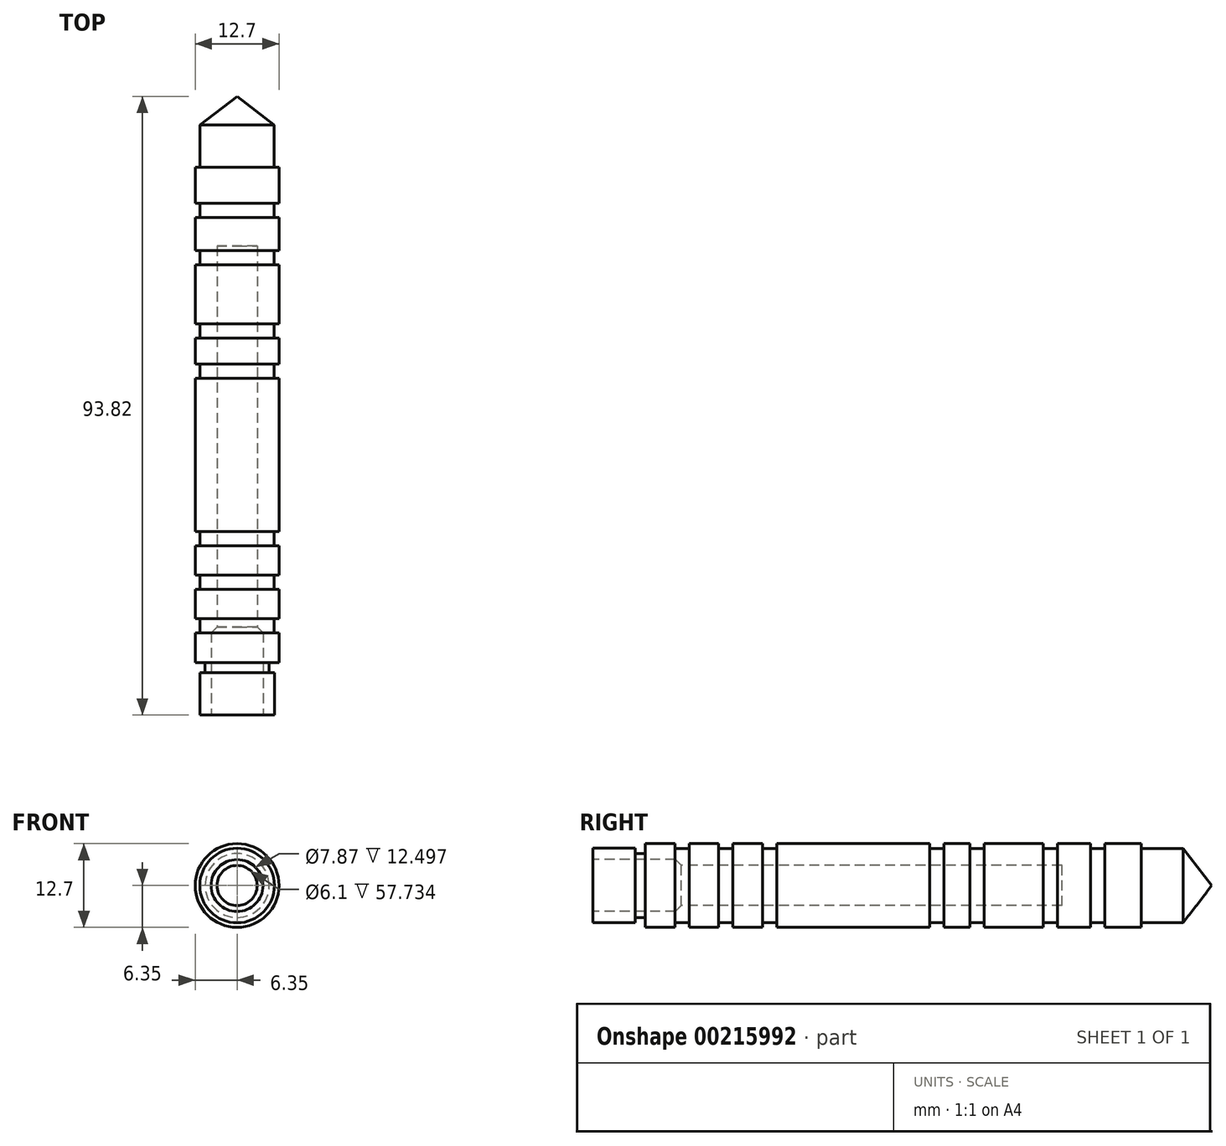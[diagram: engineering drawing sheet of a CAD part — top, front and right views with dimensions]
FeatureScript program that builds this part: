
annotation { "Feature Type Name" : "Feature", "Feature Type Description" : "" }
export const myFeature = defineFeature(function(context is Context, id is Id, definition is map)
    precondition{}
    {
        {
            var Q0;
            Q0=qCreatedBy(makeId("Front.planeOp"),FACE);
            var sketch = newSketch(context, id + "F0", { "sketchPlane" : qUnion([Q0])});
            skCircle(sketch, "E0", {"center": v(0, 0) * mm, "radius": 6.35 * mm});
            skSolve(sketch);
        }
        {
            var Q0;
            Q0 = qSketchRegion(id + "F0", true);
            extrude(context, id + "F1", {"entities" : qUnion([Q0]), "depth" : 93.83 * mm, "symmetric" : true});
        }
        {
            var Q0;
            Q0=makeQuery(id+"F1.opExtrude","CAP_FACE",FACE,{"disambiguationData":[OSD([sQuery(id+"F0.wireOp",EDGE,"E0")])],"isStart":false});
            var sketch = newSketch(context, id + "F2", { "sketchPlane" : qUnion([Q0])});
            skCircle(sketch, "E1", {"center": v(0, 0) * mm, "radius": 3.05 * mm});
            skSolve(sketch);
        }
        {
            var Q0;
            Q0 = qSketchRegion(id + "F2", true);
            extrude(context, id + "F3", {"entities" : qUnion([Q0]), "operationType" : NewBodyOperationType.REMOVE, "oppositeDirection" : true, "depth" : 71.12 * mm});
        }
        {
            var Q0;
            Q0=makeQuery(id+"F1.opExtrude","CAP_FACE",FACE,{"disambiguationData":[OSD([sQuery(id+"F0.wireOp",EDGE,"E0")])],"isStart":false});
            var sketch = newSketch(context, id + "F4", { "sketchPlane" : qUnion([Q0])});
            skCircle(sketch, "E2", {"center": v(0, 0) * mm, "radius": 3.94 * mm});
            skSolve(sketch);
        }
        {
            var Q0;
            Q0 = qSketchRegion(id + "F4", true);
            extrude(context, id + "F5", {"entities" : qUnion([Q0]), "operationType" : NewBodyOperationType.REMOVE, "oppositeDirection" : true, "depth" : 12.37 * mm});
        }
        {
            var Q0;
            Q0=makeQuery(id+"F1.opExtrude","CAP_FACE",FACE,{"disambiguationData":[OSD([sQuery(id+"F0.wireOp",EDGE,"E0")])],"isStart":false});
            var sketch = newSketch(context, id + "F6", { "sketchPlane" : qUnion([Q0])});
            skCircle(sketch, "E3", {"center": v(0, 0) * mm, "radius": 6.35 * mm});
            skCircle(sketch, "E4", {"center": v(0, 0) * mm, "radius": 5.65 * mm});
            skSolve(sketch);
        }
        {
            var Q0;
            Q0 = qSketchRegion(id + "F6", true);
            extrude(context, id + "F7", {"entities" : qUnion([Q0]), "operationType" : NewBodyOperationType.REMOVE, "oppositeDirection" : true, "depth" : 6.45 * mm});
        }
        {
            var Q0;
            Q0=makeQuery(id+"F7.boolean.opBoolean","COPY",FACE,{"derivedFrom":makeQuery(id+"F7.opExtrude","CAP_FACE",FACE,{"disambiguationData":[OSD([sQuery(id+"F6.wireOp",EDGE,"E3"),sQuery(id+"F6.wireOp",EDGE,"E4")])],"isStart":false})});
            var sketch = newSketch(context, id + "F8", { "sketchPlane" : qUnion([Q0])});
            skCircle(sketch, "E5", {"center": v(0, 0) * mm, "radius": 6.35 * mm});
            skCircle(sketch, "E6", {"center": v(0, 0) * mm, "radius": 4.85 * mm});
            skSolve(sketch);
        }
        {
            var Q0;
            Q0 = qSketchRegion(id + "F8", true);
            extrude(context, id + "F9", {"entities" : qUnion([Q0]), "operationType" : NewBodyOperationType.REMOVE, "oppositeDirection" : true, "depth" : 1.52 * mm});
        }
        {
            var Q0;
            Q0=makeQuery(id+"F5.boolean.opBoolean","INTERSECT",EDGE,{"derivedFrom":[makeQuery(id+"F3.boolean.opBoolean","COPY",FACE,{"derivedFrom":makeQuery(id+"F3.opExtrude","SWEPT_FACE",FACE,{"disambiguationData":[OSD([sQuery(id+"F2.wireOp",EDGE,"E1")])]})}),makeQuery(id+"F5.opExtrude","CAP_FACE",FACE,{"disambiguationData":[OSD([sQuery(id+"F4.wireOp",EDGE,"E2")])],"isStart":false})]});
            chamfer(context, id + "F10", {"entities" : qUnion([Q0]), "width" : 1.02 * mm, "tangentPropagation" : true});
        }
        {
            var Q0;
            Q0=makeQuery(id+"F9.boolean.opBoolean","COPY",FACE,{"derivedFrom":makeQuery(id+"F9.opExtrude","CAP_FACE",FACE,{"disambiguationData":[OSD([sQuery(id+"F8.wireOp",EDGE,"E5"),sQuery(id+"F8.wireOp",EDGE,"E6")])],"isStart":false})});
            cPlane(context, id + "F11", {"entities" : qUnion([Q0]), "cplaneType" : CPlaneType.OFFSET, "offset" : 4.47 * mm, "oppositeDirection" : true, "width" : 152.4 * mm, "height" : 152.4 * mm});
        }
        {
            var Q0;
            Q0=qCreatedBy(id+"F11.planeOp",FACE);
            var sketch = newSketch(context, id + "F12", { "sketchPlane" : qUnion([Q0])});
            skCircle(sketch, "E7", {"center": v(0, 0) * mm, "radius": 6.35 * mm});
            skCircle(sketch, "E8", {"center": v(0, 0) * mm, "radius": 5.61 * mm});
            skSolve(sketch);
        }
        {
            var Q0;
            Q0 = qSketchRegion(id + "F12", true);
            extrude(context, id + "F13", {"entities" : qUnion([Q0]), "operationType" : NewBodyOperationType.REMOVE, "oppositeDirection" : true, "depth" : 2.16 * mm});
        }
        {
            var Q0;
            Q0=makeQuery(id+"F13.boolean.opBoolean","COPY",FACE,{"derivedFrom":makeQuery(id+"F13.opExtrude","CAP_FACE",FACE,{"disambiguationData":[OSD([sQuery(id+"F12.wireOp",EDGE,"E7"),sQuery(id+"F12.wireOp",EDGE,"E8")])],"isStart":false})});
            cPlane(context, id + "F14", {"entities" : qUnion([Q0]), "cplaneType" : CPlaneType.OFFSET, "offset" : 4.47 * mm, "oppositeDirection" : true, "width" : 152.4 * mm, "height" : 152.4 * mm});
        }
        {
            var Q0;
            Q0=qCreatedBy(id+"F14.planeOp",FACE);
            var sketch = newSketch(context, id + "F15", { "sketchPlane" : qUnion([Q0])});
            skCircle(sketch, "E9", {"center": v(0, 0) * mm, "radius": 6.35 * mm});
            skCircle(sketch, "E10", {"center": v(0, 0) * mm, "radius": 5.61 * mm});
            skSolve(sketch);
        }
        {
            var Q0;
            Q0 = qSketchRegion(id + "F15", true);
            extrude(context, id + "F16", {"entities" : qUnion([Q0]), "operationType" : NewBodyOperationType.REMOVE, "oppositeDirection" : true, "depth" : 2.16 * mm});
        }
        {
            var Q0;
            Q0=makeQuery(id+"F16.boolean.opBoolean","COPY",FACE,{"derivedFrom":makeQuery(id+"F16.opExtrude","CAP_FACE",FACE,{"disambiguationData":[OSD([sQuery(id+"F15.wireOp",EDGE,"E9"),sQuery(id+"F15.wireOp",EDGE,"E10")])],"isStart":false})});
            cPlane(context, id + "F17", {"entities" : qUnion([Q0]), "cplaneType" : CPlaneType.OFFSET, "offset" : 4.47 * mm, "oppositeDirection" : true, "width" : 152.4 * mm, "height" : 152.4 * mm});
        }
        {
            var Q0;
            Q0=qCreatedBy(id+"F17.planeOp",FACE);
            var sketch = newSketch(context, id + "F18", { "sketchPlane" : qUnion([Q0])});
            skCircle(sketch, "E11", {"center": v(0, 0) * mm, "radius": 6.35 * mm});
            skCircle(sketch, "E12", {"center": v(0, 0) * mm, "radius": 5.61 * mm});
            skSolve(sketch);
        }
        {
            var Q0;
            Q0 = qSketchRegion(id + "F18", true);
            extrude(context, id + "F19", {"entities" : qUnion([Q0]), "operationType" : NewBodyOperationType.REMOVE, "oppositeDirection" : true, "depth" : 2.16 * mm});
        }
        {
            var Q0;
            Q0=makeQuery(id+"F19.boolean.opBoolean","COPY",FACE,{"derivedFrom":makeQuery(id+"F19.opExtrude","CAP_FACE",FACE,{"disambiguationData":[OSD([sQuery(id+"F18.wireOp",EDGE,"E11"),sQuery(id+"F18.wireOp",EDGE,"E12")])],"isStart":false})});
            cPlane(context, id + "F20", {"entities" : qUnion([Q0]), "cplaneType" : CPlaneType.OFFSET, "offset" : 23.2 * mm, "oppositeDirection" : true, "width" : 152.4 * mm, "height" : 152.4 * mm});
        }
        {
            var Q0;
            Q0=qCreatedBy(id+"F20.planeOp",FACE);
            var sketch = newSketch(context, id + "F21", { "sketchPlane" : qUnion([Q0])});
            skCircle(sketch, "E13", {"center": v(0, 0) * mm, "radius": 6.35 * mm});
            skCircle(sketch, "E14", {"center": v(0, 0) * mm, "radius": 5.61 * mm});
            skSolve(sketch);
        }
        {
            var Q0;
            Q0 = qSketchRegion(id + "F21", true);
            extrude(context, id + "F22", {"entities" : qUnion([Q0]), "operationType" : NewBodyOperationType.REMOVE, "oppositeDirection" : true, "depth" : 2.16 * mm});
        }
        {
            var Q0;
            Q0=makeQuery(id+"F22.boolean.opBoolean","COPY",FACE,{"derivedFrom":makeQuery(id+"F22.opExtrude","CAP_FACE",FACE,{"disambiguationData":[OSD([sQuery(id+"F21.wireOp",EDGE,"E13"),sQuery(id+"F21.wireOp",EDGE,"E14")])],"isStart":false})});
            cPlane(context, id + "F23", {"entities" : qUnion([Q0]), "cplaneType" : CPlaneType.OFFSET, "offset" : 3.96 * mm, "oppositeDirection" : true, "width" : 152.4 * mm, "height" : 152.4 * mm});
        }
        {
            var Q0;
            Q0=qCreatedBy(id+"F23.planeOp",FACE);
            var sketch = newSketch(context, id + "F24", { "sketchPlane" : qUnion([Q0])});
            skCircle(sketch, "E15", {"center": v(0, 0) * mm, "radius": 6.35 * mm});
            skCircle(sketch, "E16", {"center": v(0, 0) * mm, "radius": 5.61 * mm});
            skSolve(sketch);
        }
        {
            var Q0;
            Q0 = qSketchRegion(id + "F24", true);
            extrude(context, id + "F25", {"entities" : qUnion([Q0]), "operationType" : NewBodyOperationType.REMOVE, "oppositeDirection" : true, "depth" : 2.16 * mm});
        }
        {
            var Q0;
            Q0=makeQuery(id+"F25.boolean.opBoolean","COPY",FACE,{"derivedFrom":makeQuery(id+"F25.opExtrude","CAP_FACE",FACE,{"disambiguationData":[OSD([sQuery(id+"F24.wireOp",EDGE,"E15"),sQuery(id+"F24.wireOp",EDGE,"E16")])],"isStart":false})});
            cPlane(context, id + "F26", {"entities" : qUnion([Q0]), "cplaneType" : CPlaneType.OFFSET, "offset" : 8.97 * mm, "oppositeDirection" : true, "width" : 152.4 * mm, "height" : 152.4 * mm});
        }
        {
            var Q0;
            Q0=qCreatedBy(id+"F26.planeOp",FACE);
            var sketch = newSketch(context, id + "F27", { "sketchPlane" : qUnion([Q0])});
            skCircle(sketch, "E17", {"center": v(0, 0) * mm, "radius": 6.35 * mm});
            skCircle(sketch, "E18", {"center": v(0, 0) * mm, "radius": 5.61 * mm});
            skSolve(sketch);
        }
        {
            var Q0;
            Q0 = qSketchRegion(id + "F27", true);
            extrude(context, id + "F28", {"entities" : qUnion([Q0]), "operationType" : NewBodyOperationType.REMOVE, "oppositeDirection" : true, "depth" : 2.16 * mm});
        }
        {
            var Q0;
            Q0=makeQuery(id+"F28.boolean.opBoolean","COPY",FACE,{"derivedFrom":makeQuery(id+"F28.opExtrude","CAP_FACE",FACE,{"disambiguationData":[OSD([sQuery(id+"F27.wireOp",EDGE,"E17"),sQuery(id+"F27.wireOp",EDGE,"E18")])],"isStart":false})});
            cPlane(context, id + "F29", {"entities" : qUnion([Q0]), "cplaneType" : CPlaneType.OFFSET, "offset" : 5 * mm, "oppositeDirection" : true, "width" : 152.4 * mm, "height" : 152.4 * mm});
        }
        {
            var Q0;
            Q0=qCreatedBy(id+"F29.planeOp",FACE);
            var sketch = newSketch(context, id + "F30", { "sketchPlane" : qUnion([Q0])});
            skCircle(sketch, "E19", {"center": v(0, 0) * mm, "radius": 6.35 * mm});
            skCircle(sketch, "E20", {"center": v(0, 0) * mm, "radius": 5.61 * mm});
            skSolve(sketch);
        }
        {
            var Q0;
            Q0 = qSketchRegion(id + "F30", true);
            extrude(context, id + "F31", {"entities" : qUnion([Q0]), "operationType" : NewBodyOperationType.REMOVE, "oppositeDirection" : true, "depth" : 2.16 * mm});
        }
        {
            var Q0;
            Q0=makeQuery(id+"F31.boolean.opBoolean","COPY",FACE,{"derivedFrom":makeQuery(id+"F31.opExtrude","CAP_FACE",FACE,{"disambiguationData":[OSD([sQuery(id+"F30.wireOp",EDGE,"E19"),sQuery(id+"F30.wireOp",EDGE,"E20")])],"isStart":false})});
            cPlane(context, id + "F32", {"entities" : qUnion([Q0]), "cplaneType" : CPlaneType.OFFSET, "offset" : 5.5 * mm, "oppositeDirection" : true, "width" : 152.4 * mm, "height" : 152.4 * mm});
        }
        {
            var Q0;
            Q0=qCreatedBy(id+"F32.planeOp",FACE);
            var sketch = newSketch(context, id + "F33", { "sketchPlane" : qUnion([Q0])});
            skCircle(sketch, "E21", {"center": v(0, 0) * mm, "radius": 6.35 * mm});
            skCircle(sketch, "E22", {"center": v(0, 0) * mm, "radius": 5.61 * mm});
            skSolve(sketch);
        }
        {
            var Q0;
            Q0 = qSketchRegion(id + "F33", true);
            extrude(context, id + "F34", {"entities" : qUnion([Q0]), "operationType" : NewBodyOperationType.REMOVE, "endBound" : BoundingType.THROUGH_ALL, "oppositeDirection" : true, "depth" : 25.4 * mm});
        }
        {
            var Q0;
            Q0=makeQuery(id+"F34.boolean.opBoolean","INTERSECT",EDGE,{"derivedFrom":[makeQuery(id+"F1.opExtrude","CAP_FACE",FACE,{"disambiguationData":[OSD([sQuery(id+"F0.wireOp",EDGE,"E0")])],"isStart":true}),makeQuery(id+"F34.opExtrude","SWEPT_FACE",FACE,{"disambiguationData":[OSD([sQuery(id+"F33.wireOp",EDGE,"E22")])]})]});
            chamfer(context, id + "F35", {"entities" : qUnion([Q0]), "chamferType" : ChamferType.TWO_OFFSETS, "width1" : 4.32 * mm, "oppositeDirection" : false, "width2" : 5.61 * mm, "tangentPropagation" : true});
        }
    });
